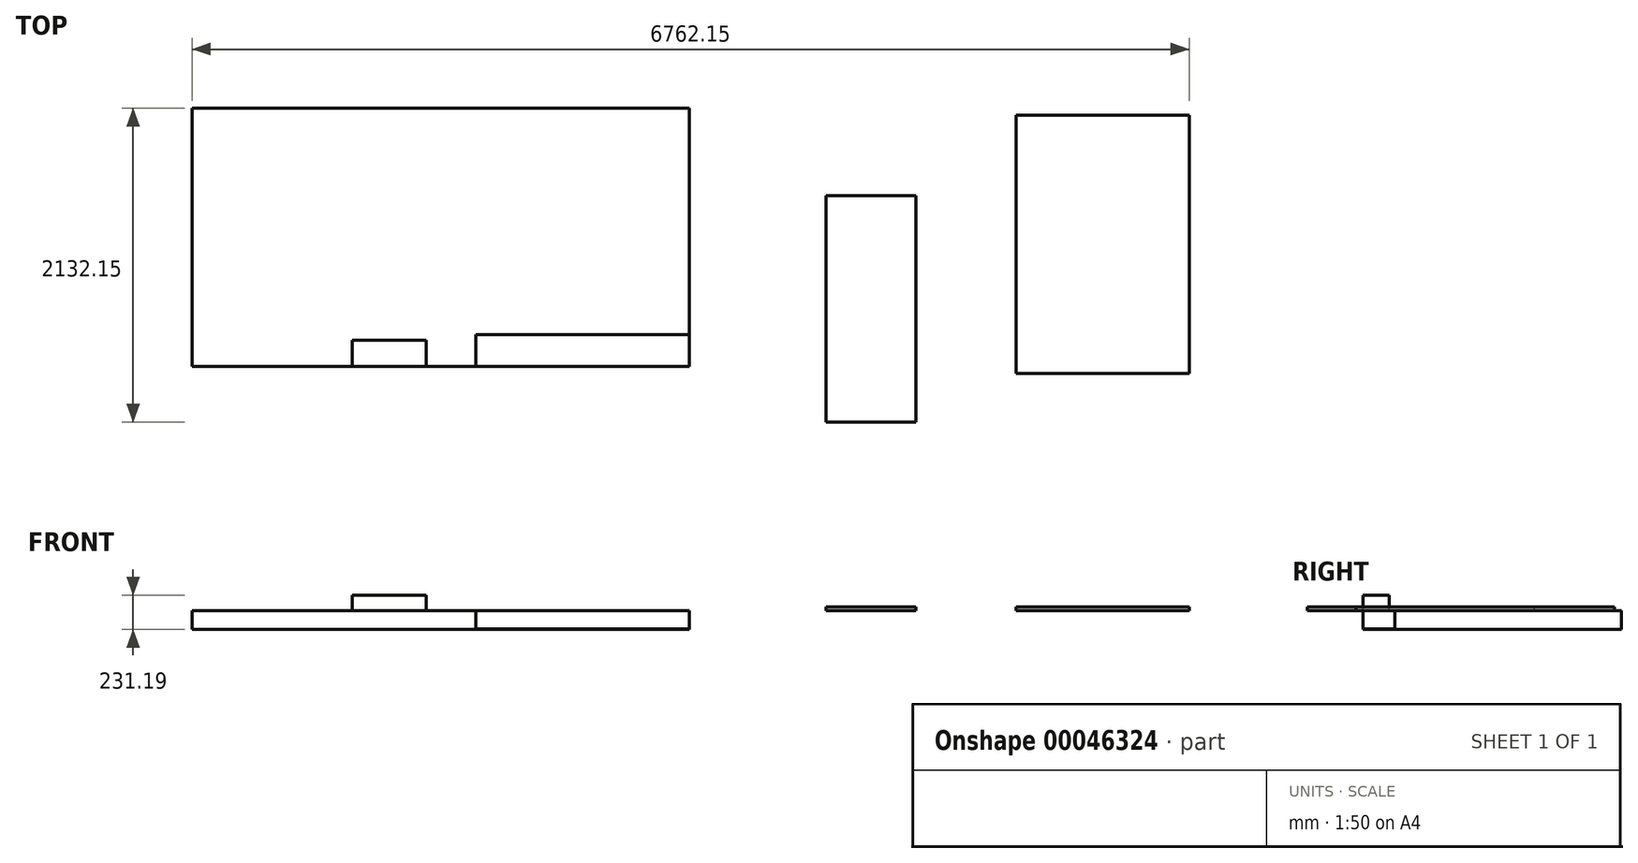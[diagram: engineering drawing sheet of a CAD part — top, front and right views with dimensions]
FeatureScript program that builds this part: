
annotation { "Feature Type Name" : "Feature", "Feature Type Description" : "" }
export const myFeature = defineFeature(function(context is Context, id is Id, definition is map)
    precondition{}
    {
        {
            var Q0;
            Q0=qCreatedBy(makeId("Top.planeOp"),FACE);
            var sketch = newSketch(context, id + "F0", { "sketchPlane" : qUnion([Q0])});
            skLineSegment(sketch, "E0.rect.bottom", {"start": v(1685.93, 876.3) * mm, "end": v(-1685.93, 876.3) * mm});
            skLineSegment(sketch, "E0.rect.top", {"start": v(1685.93, -876.3) * mm, "end": v(-1685.93, -876.3) * mm});
            skLineSegment(sketch, "E0.rect.left", {"start": v(1685.93, 876.3) * mm, "end": v(1685.93, -876.3) * mm});
            skLineSegment(sketch, "E0.rect.right", {"start": v(-1685.93, 876.3) * mm, "end": v(-1685.93, -876.3) * mm});
            skPoint(sketch, "E0.rect.middle", {"position": v(0, 0) * mm});
            skSolve(sketch);
        }
        {
            var Q0;
            Q0 = qSketchRegion(id + "F0", true);
            extrude(context, id + "F1", {"entities" : qUnion([Q0]), "oppositeDirection" : true, "depth" : 127 * mm});
        }
        {
            var Q0;
            Q0=makeQuery(id+"F1.opExtrude","CAP_FACE",FACE,{"disambiguationData":[OSD([sQuery(id+"F0.wireOp",EDGE,"E0.rect.bottom"),sQuery(id+"F0.wireOp",EDGE,"E0.rect.top"),sQuery(id+"F0.wireOp",EDGE,"E0.rect.left"),sQuery(id+"F0.wireOp",EDGE,"E0.rect.right")])],"isStart":true});
            var sketch = newSketch(context, id + "F2", { "sketchPlane" : qUnion([Q0])});
            skLineSegment(sketch, "E1.bottom", {"start": v(1685.92, -876.3) * mm, "end": v(238.13, -876.3) * mm});
            skLineSegment(sketch, "E1.top", {"start": v(1685.93, -660.4) * mm, "end": v(238.12, -660.4) * mm});
            skLineSegment(sketch, "E1.left", {"start": v(1685.93, -876.3) * mm, "end": v(1685.93, -660.4) * mm});
            skLineSegment(sketch, "E1.right", {"start": v(238.12, -876.3) * mm, "end": v(238.12, -660.4) * mm});
            skSolve(sketch);
        }
        {
            var Q0;
            Q0 = qSketchRegion(id + "F2", true);
            extrude(context, id + "F3", {"entities" : qUnion([Q0]), "operationType" : NewBodyOperationType.REMOVE, "oppositeDirection" : true, "depth" : 124.46 * mm});
        }
        {
            var Q0;
            Q0=makeQuery(id+"F1.opExtrude","SWEPT_FACE",FACE,{"disambiguationData":[OSD([sQuery(id+"F0.wireOp",EDGE,"E0.rect.top")])]});
            var sketch = newSketch(context, id + "F4", { "sketchPlane" : qUnion([Q0])});
            skLineSegment(sketch, "E2.bottom", {"start": v(-98.43, 0) * mm, "end": v(-601.25, 0) * mm});
            skLineSegment(sketch, "E2.top", {"start": v(-98.43, 104.2) * mm, "end": v(-601.25, 104.2) * mm});
            skLineSegment(sketch, "E2.left", {"start": v(-98.43, 0) * mm, "end": v(-98.43, 104.2) * mm});
            skLineSegment(sketch, "E2.right", {"start": v(-601.25, 0) * mm, "end": v(-601.25, 104.2) * mm});
            skSolve(sketch);
        }
        {
            var Q0;
            Q0 = qSketchRegion(id + "F4", true);
            extrude(context, id + "F5", {"entities" : qUnion([Q0]), "oppositeDirection" : true, "depth" : 177.8 * mm});
        }
        {
            var Q0;
            {var subQ4=sQuery(id+"F2.wireOp",EDGE,"E1.top");Q0=makeQuery(id+"F2.imprint","IMPRINT",FACE,{"disambiguationData":[TD([[makeQuery(id+"F2.imprint","IMPRINT",EDGE,{"derivedFrom":subQ4}),-1.0]])]});}
            var sketch = newSketch(context, id + "F6", { "sketchPlane" : qUnion([Q0])});
            skLineSegment(sketch, "E3.bottom", {"start": v(2612.17, 280.85) * mm, "end": v(3221.77, 280.85) * mm});
            skLineSegment(sketch, "E3.top", {"start": v(2612.17, -1255.85) * mm, "end": v(3221.77, -1255.85) * mm});
            skLineSegment(sketch, "E3.left", {"start": v(2612.17, 280.85) * mm, "end": v(2612.17, -1255.85) * mm});
            skLineSegment(sketch, "E3.right", {"start": v(3221.77, 280.85) * mm, "end": v(3221.77, -1255.85) * mm});
            skSolve(sketch);
        }
        {
            var Q0;
            Q0 = qSketchRegion(id + "F6", true);
            extrude(context, id + "F7", {"entities" : qUnion([Q0]), "depth" : 25.4 * mm});
        }
        {
            var Q0;
            {var subQ4=sQuery(id+"F2.wireOp",EDGE,"E1.top");Q0=makeQuery(id+"F2.imprint","IMPRINT",FACE,{"disambiguationData":[TD([[makeQuery(id+"F2.imprint","IMPRINT",EDGE,{"derivedFrom":subQ4}),-1.0]])]});}
            var sketch = newSketch(context, id + "F8", { "sketchPlane" : qUnion([Q0])});
            skLineSegment(sketch, "E4.bottom", {"start": v(3901.48, -925.66) * mm, "end": v(5076.23, -925.66) * mm});
            skLineSegment(sketch, "E4.top", {"start": v(3901.48, 826.94) * mm, "end": v(5076.23, 826.94) * mm});
            skLineSegment(sketch, "E4.left", {"start": v(3901.48, -925.66) * mm, "end": v(3901.48, 826.94) * mm});
            skLineSegment(sketch, "E4.right", {"start": v(5076.23, -925.66) * mm, "end": v(5076.23, 826.94) * mm});
            skSolve(sketch);
        }
        {
            var Q0;
            Q0 = qSketchRegion(id + "F8", true);
            extrude(context, id + "F9", {"entities" : qUnion([Q0]), "depth" : 25.4 * mm});
        }
    });
